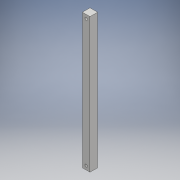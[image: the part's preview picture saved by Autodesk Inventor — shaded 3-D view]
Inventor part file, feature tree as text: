
AUTODESK INVENTOR PART (.ipt)
format: ipt  version: 2018 (Build 220112000, 112)  size: 104,448 bytes
history: native  units: mm
features: sketch x2, extrude x1, hole x1
ambient origin geometry x8: Origin, YZ Plane, XZ Plane, XY Plane, X Axis, Y Axis, Z Axis, Center Point
bodies: Body1 (feature_tree)
feature tree (4):
  extrude  "押し出し2"  Depth=30.0mm
  hole  "穴2"  [1 undecoded]
  sketch  "スケッチ4"
  sketch  "スケッチ5"
note: 1 required parameter value undecoded (feature->parameter linkage not recoverable at this tier; creation-order binding heuristic only, values carry confidence <= 0.55)
